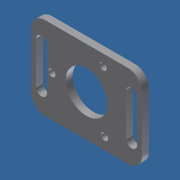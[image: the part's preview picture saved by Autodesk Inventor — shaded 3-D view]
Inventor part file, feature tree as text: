
AUTODESK INVENTOR PART (.ipt)
format: ipt  version: 2012 (Build 160160000, 160)  size: 122,368 bytes
history: native  units: in
note: dims shown in document units (in); Inventor stores cm internally (conversion verified against a paired STEP export)
features: sketch x1, extrude x1, hole x1, fillet x1
ambient origin geometry x8: Origin, YZ Plane, XZ Plane, XY Plane, X Axis, Y Axis, Z Axis, Center Point
bodies: Solid1 (feature_tree)
feature tree (4):
  sketch  "Sketch1"  dims[d0=0.75in d1=0.75in d2=1.5in d3=1.125in d4=2.25in d5=1.25in d6=1.1811in d8=360.0deg d11=0.1875in d12=0.75in d13=0.375in d14=0.2in d15=0.75in d16=0.2in d17=0.1875in d18=0.125in d19=0.0in d20=0.128in d21=0.75in d22=0.375in d23=0.25in d24=0.5635in d25=1.0in d26=0.8108in d27=0.25in d33=0.325in]
  extrude  "Extrusion1"  Depth=0.75in
  hole  "Hole1"  [1 undecoded]
  fillet  "Fillet1"  Radius=1.125in
note: 1 required parameter value undecoded (feature->parameter linkage not recoverable at this tier; creation-order binding heuristic only, values carry confidence <= 0.55)
